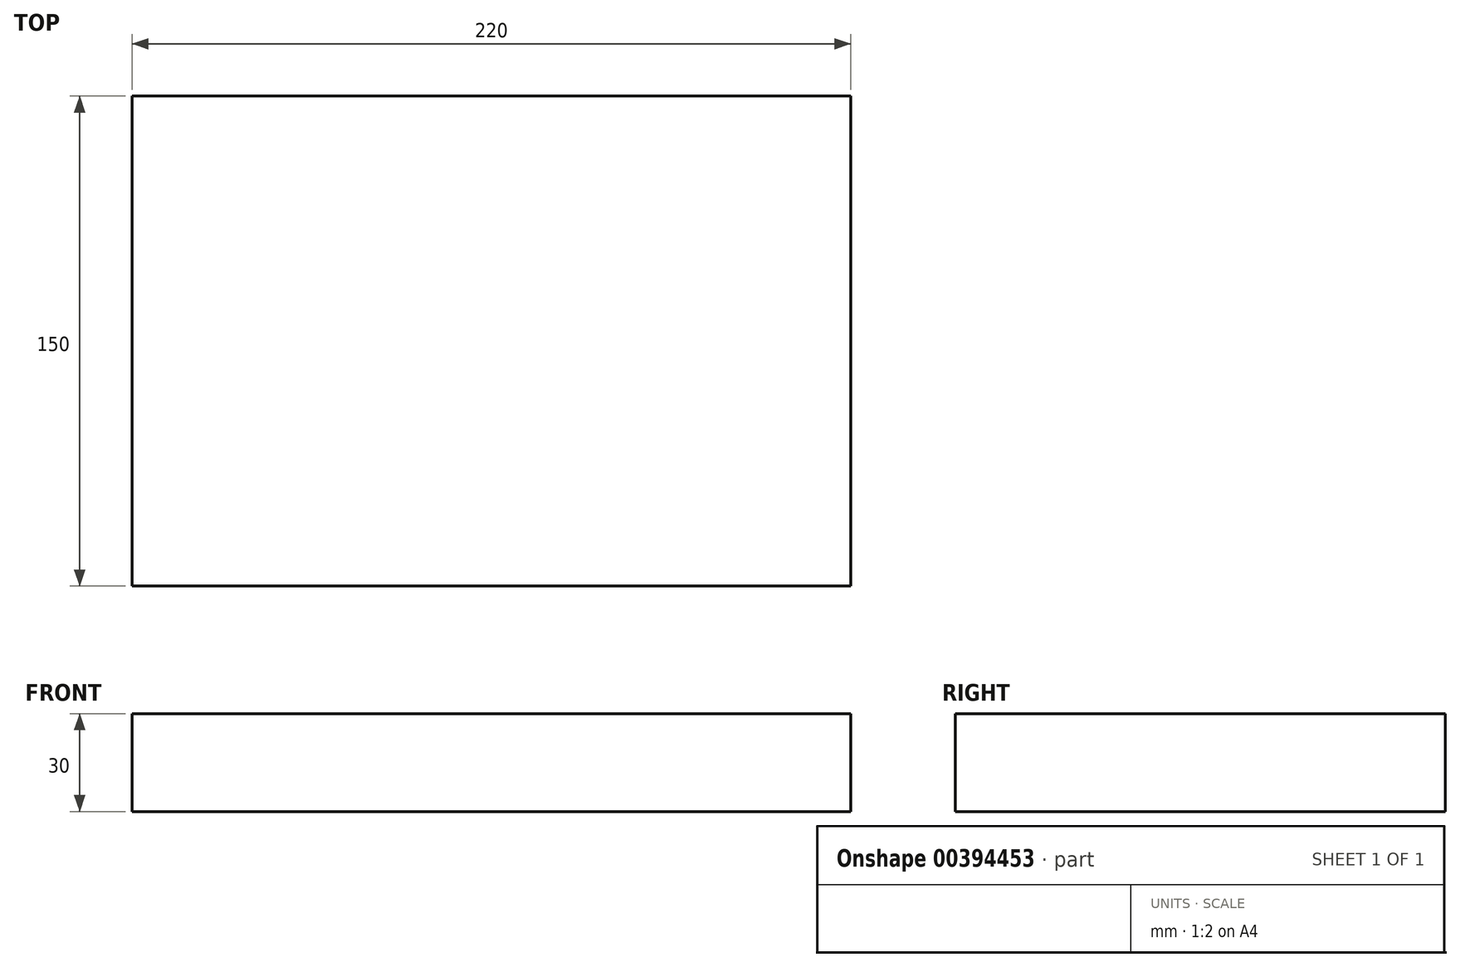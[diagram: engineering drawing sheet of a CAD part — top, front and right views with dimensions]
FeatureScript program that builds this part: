
annotation { "Feature Type Name" : "Feature", "Feature Type Description" : "" }
export const myFeature = defineFeature(function(context is Context, id is Id, definition is map)
    precondition{}
    {
        {
            var Q0;
            Q0=qCreatedBy(makeId("Top.planeOp"),FACE);
            var sketch = newSketch(context, id + "F0", { "sketchPlane" : qUnion([Q0])});
            skLineSegment(sketch, "E0.bottom", {"start": v(110, -75) * mm, "end": v(-110, -75) * mm});
            skLineSegment(sketch, "E0.top", {"start": v(110, 75) * mm, "end": v(-110, 75) * mm});
            skLineSegment(sketch, "E0.left", {"start": v(110, -75) * mm, "end": v(110, 75) * mm});
            skLineSegment(sketch, "E0.right", {"start": v(-110, -75) * mm, "end": v(-110, 75) * mm});
            skPoint(sketch, "E0.middle", {"position": v(0, 0) * mm});
            skSolve(sketch);
        }
        {
            var Q0;
            Q0 = qSketchRegion(id + "F0", true);
            extrude(context, id + "F1", {"entities" : qUnion([Q0]), "depth" : 30 * mm});
        }
    });
